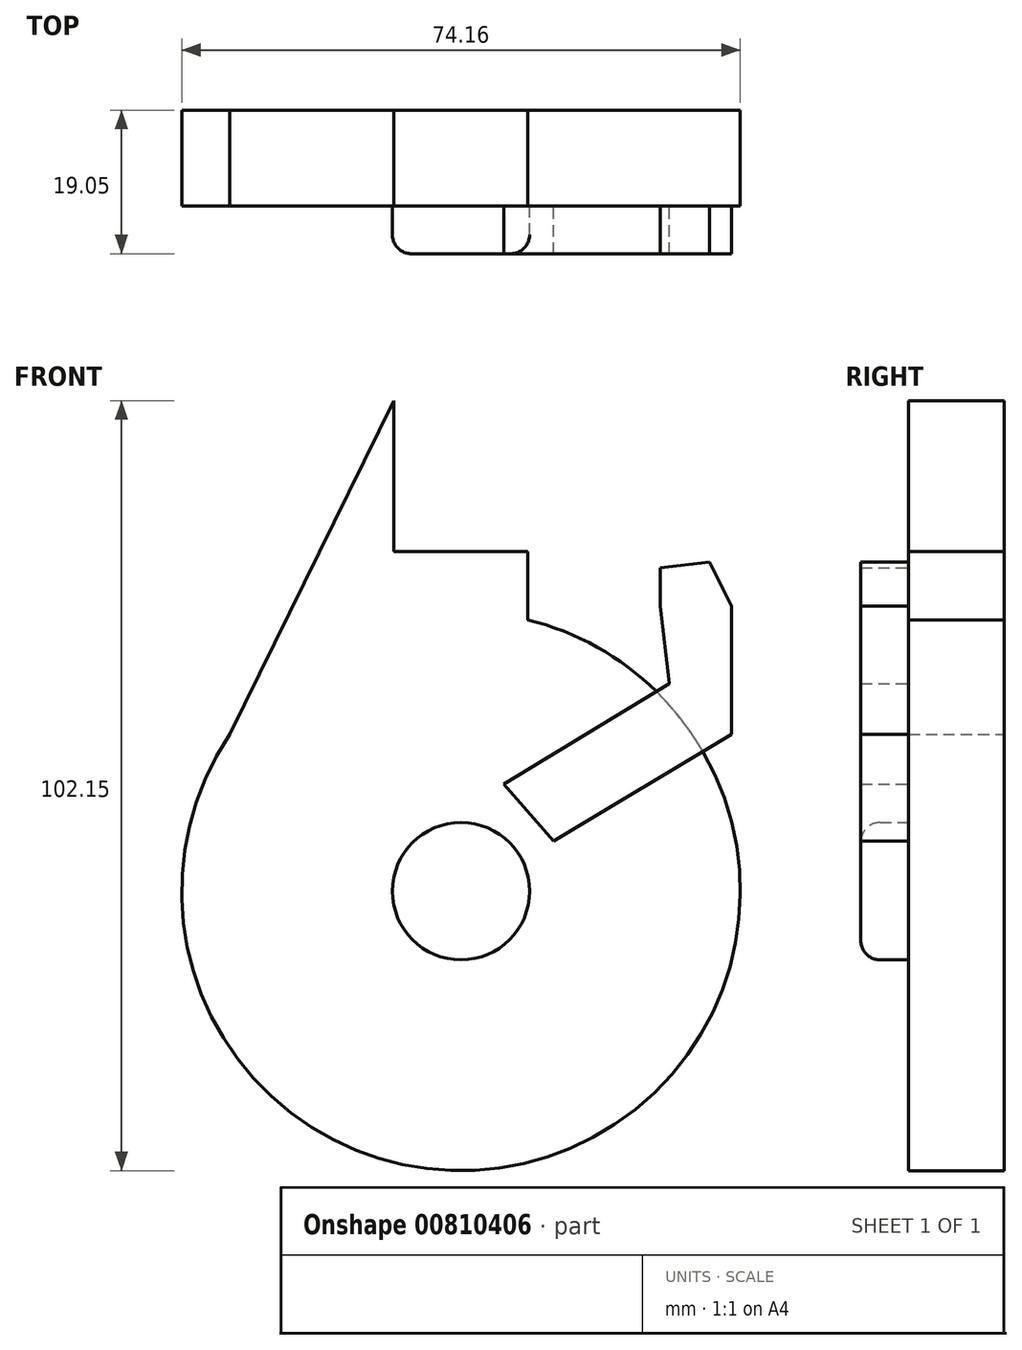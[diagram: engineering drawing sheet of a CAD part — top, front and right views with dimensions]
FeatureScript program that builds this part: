
annotation { "Feature Type Name" : "Feature", "Feature Type Description" : "" }
export const myFeature = defineFeature(function(context is Context, id is Id, definition is map)
    precondition{}
    {
        {
            var Q0;
            Q0=qCreatedBy(makeId("Front.planeOp"),FACE);
            var sketch = newSketch(context, id + "F0", { "sketchPlane" : qUnion([Q0])});
            skCircle(sketch, "E0", {"center": v(0, 0) * mm, "radius": 37.08 * mm});
            skLineSegment(sketch, "E1", {"start": v(-8.9, 36) * mm, "end": v(-8.9, 65.07) * mm});
            skLineSegment(sketch, "E2", {"start": v(-8.9, 65.07) * mm, "end": v(-30.7, 20.8) * mm});
            skLineSegment(sketch, "E3", {"start": v(8.89, 36) * mm, "end": v(8.89, 65.07) * mm});
            skLineSegment(sketch, "E4", {"start": v(8.89, 65.07) * mm, "end": v(31.05, 20.8) * mm});
            skLineSegment(sketch, "E5.bottom", {"start": v(-8.9, 45.07) * mm, "end": v(8.87, 45.07) * mm});
            skLineSegment(sketch, "E5.top", {"start": v(-8.9, 0) * mm, "end": v(8.87, 0) * mm});
            skLineSegment(sketch, "E5.left", {"start": v(-8.9, 45.07) * mm, "end": v(-8.9, 0) * mm});
            skLineSegment(sketch, "E5.right", {"start": v(8.87, 45.07) * mm, "end": v(8.87, 0) * mm});
            skLineSegment(sketch, "E6", {"start": v(8.89, 65.07) * mm, "end": v(8.89, 36) * mm});
            skLineSegment(sketch, "E7", {"start": v(31.05, 20.8) * mm, "end": v(8.89, 65.07) * mm});
            skLineSegment(sketch, "E8", {"start": v(8.89, 36) * mm, "end": v(31.05, 20.8) * mm});
            skSolve(sketch);
        }
        {
            var Q0;
            {var subQ5=sQuery(id+"F0.wireOp",EDGE,"E5.top");Q0=makeQuery(id+"F0.imprint","IMPRINT",FACE,{"disambiguationData":[TD([[makeQuery(id+"F0.imprint","IMPRINT",EDGE,{"derivedFrom":subQ5}),-1.0]])]});}
            var Q1;
            {var subQ4=sQuery(id+"F0.wireOp",EDGE,"E1");Q1=makeQuery(id+"F0.imprint","IMPRINT",FACE,{"disambiguationData":[TD([[makeQuery(id+"F0.imprint","IMPRINT",EDGE,{"derivedFrom":subQ4}),1.0]])]});}
            var Q2;
            {var subQ5=sQuery(id+"F0.wireOp",EDGE,"E5.bottom");Q2=makeQuery(id+"F0.imprint","IMPRINT",FACE,{"disambiguationData":[TD([[makeQuery(id+"F0.imprint","IMPRINT",EDGE,{"derivedFrom":subQ5}),-1.0]])]});}
            var Q3;
            {var subQ5=sQuery(id+"F0.wireOp",EDGE,"E5.top");Q3=makeQuery(id+"F0.imprint","IMPRINT",FACE,{"disambiguationData":[TD([[makeQuery(id+"F0.imprint","IMPRINT",EDGE,{"derivedFrom":subQ5}),1.0]])]});}
            var Q4;
            {var subQ1=sQuery(id+"F0.wireOp",EDGE,"E6");Q4=makeQuery(id+"F0.imprint","IMPRINT",FACE,{"disambiguationData":[TD([[makeQuery(id+"F0.imprint","IMPRINT",EDGE,{"derivedFrom":subQ1}),1.0]])]});}
            var Q5;
            {var subQ0=sQuery(id+"F0.wireOp",EDGE,"E8");var subQ1=sQuery(id+"F0.wireOp",EDGE,"E0");var subQ3=makeQuery(id+"F0.imprint","INTERSECT",VERTEX,{"derivedFrom":[subQ1,subQ0]});Q5=makeQuery(id+"F0.imprint","IMPRINT",FACE,{"disambiguationData":[TD([[makeQuery(id+"F0.imprint","IMPRINT",EDGE,{"disambiguationData":[TD([[subQ3,-1.0]])],"derivedFrom":subQ1}),1.0]])]});}
            extrude(context, id + "F1", {"entities" : qUnion([Q0, Q1, Q2, Q3, Q4, Q5]), "depth" : 12.7 * mm, "offsetDistance" : 25.4 * mm});
        }
        {
            var Q0;
            Q0=makeQuery(id+"F1.opExtrude","CAP_FACE",FACE,{"disambiguationData":[OSD([sQuery(id+"F0.wireOp",EDGE,"E0"),sQuery(id+"F0.wireOp",EDGE,"E1"),sQuery(id+"F0.wireOp",EDGE,"E2"),sQuery(id+"F0.wireOp",EDGE,"E5.bottom"),sQuery(id+"F0.wireOp",EDGE,"E5.right"),sQuery(id+"F0.wireOp",EDGE,"E6"),sQuery(id+"F0.wireOp",EDGE,"E7"),sQuery(id+"F0.wireOp",EDGE,"E8")])],"isStart":false});
            var sketch = newSketch(context, id + "F2", { "sketchPlane" : qUnion([Q0])});
            skCircle(sketch, "E9", {"center": v(0, 0) * mm, "radius": 9.1 * mm});
            skLineSegment(sketch, "E10", {"start": v(5.7, 14.2) * mm, "end": v(12.3, 6.64) * mm});
            skLineSegment(sketch, "E11", {"start": v(12.3, 6.64) * mm, "end": v(35.9, 20.8) * mm});
            skLineSegment(sketch, "E12", {"start": v(35.9, 20.8) * mm, "end": v(27.67, 27.55) * mm});
            skLineSegment(sketch, "E13", {"start": v(27.67, 27.55) * mm, "end": v(5.7, 14.2) * mm});
            skLineSegment(sketch, "E14", {"start": v(35.9, 20.8) * mm, "end": v(35.9, 37.8) * mm});
            skLineSegment(sketch, "E15", {"start": v(35.9, 37.8) * mm, "end": v(32.98, 43.65) * mm});
            skLineSegment(sketch, "E16", {"start": v(32.98, 43.65) * mm, "end": v(26.47, 42.93) * mm});
            skPoint(sketch, "E16.endSnap0", {"position": v(19.97, 42.93) * mm});
            skLineSegment(sketch, "E17", {"start": v(26.47, 42.93) * mm, "end": v(26.47, 37.8) * mm});
            skLineSegment(sketch, "E18", {"start": v(26.47, 37.8) * mm, "end": v(27.67, 27.55) * mm});
            skLineSegment(sketch, "E19", {"start": v(9.1, 0) * mm, "end": v(8.34, -3.67) * mm});
            skSolve(sketch);
        }
        {
            var Q0;
            Q0 = qSketchRegion(id + "F2", true);
            extrude(context, id + "F3", {"entities" : qUnion([Q0]), "operationType" : NewBodyOperationType.ADD, "depth" : 6.35 * mm, "offsetDistance" : 25.4 * mm});
        }
        {
            var Q0;
            Q0=makeQuery(id+"F3.opExtrude","CAP_EDGE",EDGE,{"disambiguationData":[OSD([sQuery(id+"F2.wireOp",EDGE,"E9")])],"isStart":false});
            fillet(context, id + "F4", {"entities" : qUnion([Q0]), "radius" : 2.54 * mm, "tangentPropagation" : true, "allowEdgeOverflow" : false});
        }
    });
